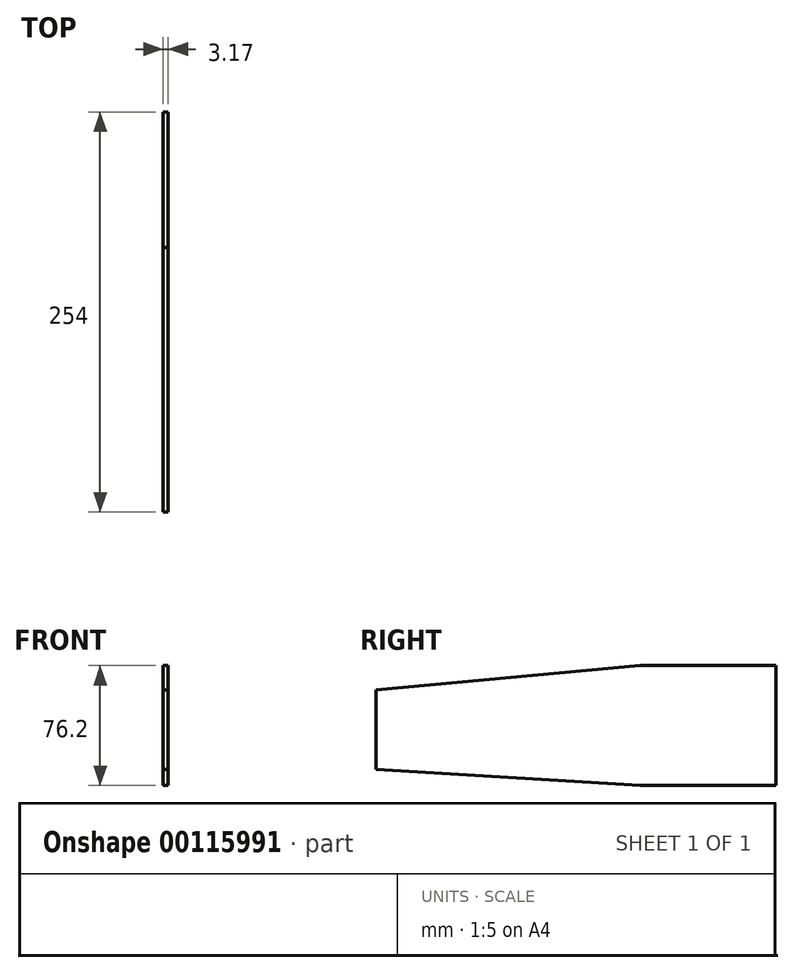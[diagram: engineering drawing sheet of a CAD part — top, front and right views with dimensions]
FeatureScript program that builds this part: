
annotation { "Feature Type Name" : "Feature", "Feature Type Description" : "" }
export const myFeature = defineFeature(function(context is Context, id is Id, definition is map)
    precondition{}
    {
        {
            var Q0;
            Q0=qCreatedBy(makeId("Right.planeOp"),FACE);
            var sketch = newSketch(context, id + "F0", { "sketchPlane" : qUnion([Q0])});
            skLineSegment(sketch, "E0", {"start": v(26.53, 38.96) * mm, "end": v(-141.58, 23.46) * mm});
            skLineSegment(sketch, "E1.MirrorCS", {"start": v(26.53, -37.24) * mm, "end": v(-141.58, -26.95) * mm});
            skLineSegment(sketch, "E2.bottom", {"start": v(26.53, 38.96) * mm, "end": v(112.42, 38.96) * mm});
            skLineSegment(sketch, "E2.top", {"start": v(26.53, -37.24) * mm, "end": v(112.42, -37.24) * mm});
            skLineSegment(sketch, "E2.right", {"start": v(112.42, 38.96) * mm, "end": v(112.42, -37.24) * mm});
            skLineSegment(sketch, "E3", {"start": v(-141.58, 23.46) * mm, "end": v(-141.58, -26.95) * mm});
            skSolve(sketch);
        }
        {
            var Q0;
            Q0=makeQuery(id+"F0.imprint","IMPRINT",FACE,{"disambiguationData":[TD([[makeQuery(id+"F0.imprint","IMPRINT",EDGE,{"derivedFrom":sQuery(id+"F0.wireOp",EDGE,"E0")}),1.0]])]});
            extrude(context, id + "F1", {"entities" : qUnion([Q0]), "depth" : 3.17 * mm});
        }
    });
